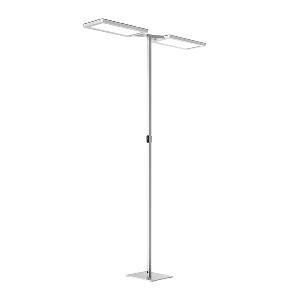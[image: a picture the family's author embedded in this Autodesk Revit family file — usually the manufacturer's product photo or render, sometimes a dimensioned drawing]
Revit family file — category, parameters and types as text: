
# Revit family: yara_doublet_-_yts_2_15000_840_r_sr_cee_s0_c_114268000-00808488_4ca8
name_source: partatom
category: Lighting Fixtures
units: mm (PartAtom-declared; Revit-internal decimal feet)

## family parameters
Cut with Voids When Loaded = No
Host = Face
Light Source = No
Part Type = Normal
Room Calculation Point = No
Round Connector Dimension = Use Diameter
Shared = No

## types (1)
- YARA.doubleT - YTS 2/15000/840/R/SR/CEE/S0/C (1 x LED, 15000 lm, 4000K)
    Apparent Load = 214 VA
    Approval mark = CE
    CIE Flux Codes = 58 87 97 13 100
    Color Rendering = 80-89
    Color Temperature = 4000K
    Control Gear = Electronic ballast
    Default Elevation = 1800 mm
    Description = YTS 2/15000/840/R/SR/CEE/S0/R|Free-standing luminaire|light source: LED|work equipment: Electronic ballast DALI|connected load: 220-240 V, 50/60 Hz|Power consumption: approx. 210 W|power factor: approx. 0,966|luminous flux: 30000 lm|luminous efficacy: 142 lm/W|light distribution: Direct/indirect|direct ratio: approx. 13 %|colour temperature: Cold white, ca. 4000 K|color rendering index (CRI): >= 80|chromaticity tolerance:  3 SDCM|technology: Presence and daylight sensor control (PIR)|operation: Wireless switch|luminaire body|material: Aluminium/plastic|surface: Powder coatet|colour: Silver metallic|lamp cover: Acrylic (PMMA), Satine, Structured|tubular section|material: Steel tube|surface: Powder-coated|Form: Tubular section upright|colour of tubular section: Silver metallic|luminaire base|Form: Rectangular flat|weight (net): approx. 24.0 kg|mains lead: 3.00 m Mains plug CEE 7/VII|Fastening: Floor standing base|glare control: Conical prismatic screen|luminance(L65): <= 2700 cd/m|unified glare rating(4H 8H): <=  16|special features: App control, Asymmetric radiation, Direct and indirect lighting component with edge light and light guidetechnology for a homogeneous light exit, Flicker-free, Magnetic control panel, freely positionable, PIR movement and daylight sensor, TALK Bluetooth|Approval mark: VDE - ENEC|
    Frequency = 50 Hz, 60 Hz
    Height = 24 mm  [stored 0.0787402 ft]
    Lamp = 1 x LED
    Lamp Light Flux = 15000 lm
    Lamp count = 1
    Length = 690 mm
    Luminous efficacy = 140 lm/W
    Manufacturer = Waldmann
    ModVariant = No
    Model = 114268000-00808488
    Mounting Place = Floor
    Mounting Type = Freestanding
    Number of Poles = 1
    OnlyDefault = Yes
    Power Factor = 1
    Product Name = YARA.doubleT - YTS 2/15000/840/R/SR/CEE/S0/C
    Product group = Free standing luminaire
    ProductGroupID = 13
    Protection Class = Protection class I
    Protection Degree = IP 20
    RLX_Detail_Level = 1
    RlxData = <blob elided: 63413 chars, md5=a2a9cdca>
    Socket = socket
    Standby Power = 0 W
    System Light Flux = 30000 lm
    System Power = 214 W
    Type Comments = Product without accessories
    Type Image = yts-r-sr-r.jpg
    URL = http://relux.com
    VarID = ---
    Voltage = 230 V
    Voltage Range = 220-240 V
    Weight = 0.00 kg
    Width = 358 mm

note: [stored X ft] marks values corroborated as IEEE doubles in the binary element streams (Revit-internal decimal feet)

## geometry (parser evidence)
native form markers: Blend x4, Sweep x23
no freeform markers — native parametric forms only
